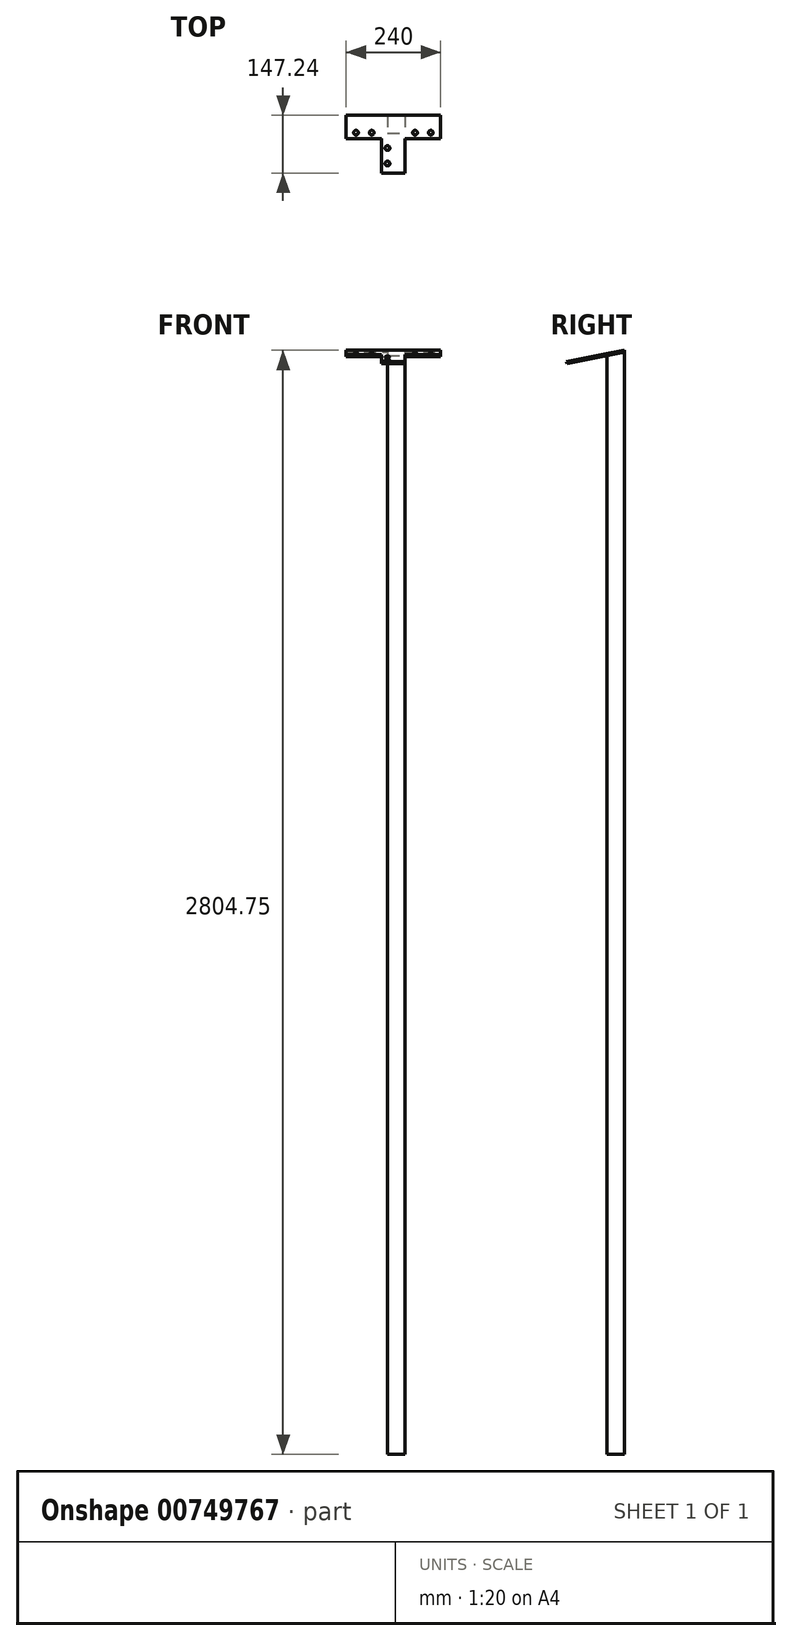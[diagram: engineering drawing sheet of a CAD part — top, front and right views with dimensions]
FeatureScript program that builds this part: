
annotation { "Feature Type Name" : "Feature", "Feature Type Description" : "" }
export const myFeature = defineFeature(function(context is Context, id is Id, definition is map)
    precondition{}
    {
        {
            var Q0;
            Q0=qCreatedBy(makeId("Top.planeOp"),FACE);
            var sketch = newSketch(context, id + "F0", { "sketchPlane" : qUnion([Q0])});
            skLineSegment(sketch, "E0.bottom", {"start": v(22.5, -22.5) * mm, "end": v(-22.5, -22.5) * mm});
            skLineSegment(sketch, "E0.top", {"start": v(22.5, 22.5) * mm, "end": v(-22.5, 22.5) * mm});
            skLineSegment(sketch, "E0.left", {"start": v(22.5, -22.5) * mm, "end": v(22.5, 22.5) * mm});
            skLineSegment(sketch, "E0.right", {"start": v(-22.5, -22.5) * mm, "end": v(-22.5, 22.5) * mm});
            skPoint(sketch, "E0.middle", {"position": v(0, 0) * mm});
            skSolve(sketch);
        }
        {
            var Q0;
            Q0=qSketchRegion(id+"F0",true);
            extrude(context, id + "F1", {"entities" : qUnion([Q0]), "depth" : 3330 * mm, "offsetDistance" : 25 * mm});
        }
        {
            var Q0;
            Q0=qCreatedBy(makeId("Top.planeOp"),FACE);
            cPlane(context, id + "F2", {"entities" : qUnion([Q0]), "cplaneType" : CPlaneType.OFFSET, "offset" : 965 * mm, "width" : 150 * mm, "height" : 150 * mm});
        }
        {
            var Q0;
            Q0=qCreatedBy(id+"F2.planeOp",FACE);
            var sketch = newSketch(context, id + "F3", { "sketchPlane" : qUnion([Q0])});
            skLineSegment(sketch, "E1", {"start": v(0, 0) * mm, "end": v(22.5, 0) * mm});
            skLineSegment(sketch, "E2", {"start": v(22.5, 0) * mm, "end": v(32.5, 0) * mm});
            skCircle(sketch, "E3", {"center": v(32.5, 0) * mm, "radius": 10 * mm});
            skLineSegment(sketch, "E4", {"start": v(32.5, 0) * mm, "end": v(32.5, 2) * mm});
            skLineSegment(sketch, "E5", {"start": v(32.5, 0) * mm, "end": v(32.5, -2) * mm});
            skLineSegment(sketch, "E6", {"start": v(32.5, -2) * mm, "end": v(22.5, -2) * mm});
            skLineSegment(sketch, "E7", {"start": v(32.5, 2) * mm, "end": v(22.5, 2) * mm});
            skLineSegment(sketch, "E8", {"start": v(0, 0) * mm, "end": v(-22.5, 0) * mm});
            skLineSegment(sketch, "E9", {"start": v(-22.5, 0) * mm, "end": v(-32.5, 0) * mm});
            skCircle(sketch, "E10", {"center": v(-32.5, 0) * mm, "radius": 10 * mm});
            skSolve(sketch);
        }
        {
            var Q0;
            Q0=makeQuery(id+"F1.opExtrude","CAP_EDGE",EDGE,{"disambiguationData":[OSD([sQuery(id+"F0.wireOp",EDGE,"E0.bottom")])],"isStart":false});
            cPlane(context, id + "F4", {"entities" : qUnion([Q0]), "cplaneType" : CPlaneType.LINE_ANGLE, "offset" : 25 * mm, "angle" : 101 * degree, "oppositeDirection" : true, "width" : 150 * mm, "height" : 150 * mm});
        }
        {
            var Q0;
            Q0=makeQuery(id+"F1.opExtrude","CAP_FACE",FACE,{"disambiguationData":[OSD([sQuery(id+"F0.wireOp",EDGE,"E0.bottom"),sQuery(id+"F0.wireOp",EDGE,"E0.top"),sQuery(id+"F0.wireOp",EDGE,"E0.left"),sQuery(id+"F0.wireOp",EDGE,"E0.right")])],"isStart":false});
            var sketch = newSketch(context, id + "F5", { "sketchPlane" : qUnion([Q0])});
            skLineSegment(sketch, "E11.bottom", {"start": v(-22.5, 22.5) * mm, "end": v(22.5, 22.5) * mm});
            skLineSegment(sketch, "E11.top", {"start": v(-22.5, -22.5) * mm, "end": v(22.5, -22.5) * mm});
            skLineSegment(sketch, "E11.left", {"start": v(-22.5, 22.5) * mm, "end": v(-22.5, -22.5) * mm});
            skLineSegment(sketch, "E11.right", {"start": v(22.5, 22.5) * mm, "end": v(22.5, -22.5) * mm});
            skSolve(sketch);
        }
        {
            var Q0;
            Q0=qCreatedBy(id+"F4.planeOp",FACE);
            var sketch = newSketch(context, id + "F6", { "sketchPlane" : qUnion([Q0])});
            skLineSegment(sketch, "E12.bottom", {"start": v(-22.5, -659.15) * mm, "end": v(22.5, -659.15) * mm});
            skLineSegment(sketch, "E12.top", {"start": v(-22.5, -613.3) * mm, "end": v(22.5, -613.3) * mm});
            skLineSegment(sketch, "E12.left", {"start": v(-22.5, -659.15) * mm, "end": v(-22.5, -613.3) * mm});
            skLineSegment(sketch, "E12.right", {"start": v(22.5, -659.15) * mm, "end": v(22.5, -613.3) * mm});
            skSolve(sketch);
        }
        {
            var Q0;
            Q0=makeQuery(id+"F6.imprint","IMPRINT",FACE,{"disambiguationData":[TD([[makeQuery(id+"F6.imprint","IMPRINT",EDGE,{"derivedFrom":sQuery(id+"F6.wireOp",EDGE,"E12.bottom")}),1.0]])]});
            extrude(context, id + "F7", {"entities" : qUnion([Q0]), "operationType" : NewBodyOperationType.ADD, "depth" : 25 * mm, "offsetDistance" : 25 * mm});
        }
        {
            var Q0;
            Q0=qCreatedBy(id+"F4.planeOp",FACE);
            var sketch = newSketch(context, id + "F8", { "sketchPlane" : qUnion([Q0])});
            skLineSegment(sketch, "E13.bottom", {"start": v(-37.5, -659.15) * mm, "end": v(22.5, -659.15) * mm});
            skLineSegment(sketch, "E13.top", {"start": v(-37.5, -599.15) * mm, "end": v(22.5, -599.15) * mm});
            skLineSegment(sketch, "E13.left", {"start": v(-37.5, -659.15) * mm, "end": v(-37.5, -599.15) * mm});
            skLineSegment(sketch, "E13.right", {"start": v(22.5, -659.15) * mm, "end": v(22.5, -599.15) * mm});
            skLineSegment(sketch, "E14.bottom", {"start": v(22.5, -659.15) * mm, "end": v(112.5, -659.15) * mm});
            skLineSegment(sketch, "E14.top", {"start": v(22.5, -599.15) * mm, "end": v(112.5, -599.15) * mm});
            skLineSegment(sketch, "E14.right", {"start": v(112.5, -659.15) * mm, "end": v(112.5, -599.15) * mm});
            skLineSegment(sketch, "E15.top", {"start": v(-37.5, -509.15) * mm, "end": v(22.5, -509.15) * mm});
            skLineSegment(sketch, "E15.left", {"start": v(-37.5, -599.15) * mm, "end": v(-37.5, -509.15) * mm});
            skLineSegment(sketch, "E15.right", {"start": v(22.5, -599.15) * mm, "end": v(22.5, -509.15) * mm});
            skLineSegment(sketch, "E16", {"start": v(-37.5, -659.15) * mm, "end": v(-37.5, -509.15) * mm});
            skLineSegment(sketch, "E17", {"start": v(-37.5, -659.15) * mm, "end": v(-127.5, -659.15) * mm});
            skLineSegment(sketch, "E18", {"start": v(-127.5, -659.15) * mm, "end": v(-127.5, -599.15) * mm});
            skLineSegment(sketch, "E19", {"start": v(-127.5, -599.15) * mm, "end": v(-37.5, -599.15) * mm});
            skPoint(sketch, "E20", {"position": v(7.5, -659.15) * mm});
            skSolve(sketch);
        }
        {
            var Q0;
            Q0=qSketchRegion(id+"F8",true);
            extrude(context, id + "F9", {"entities" : qUnion([Q0]), "operationType" : NewBodyOperationType.ADD, "depth" : 5 * mm, "offsetDistance" : 25 * mm});
        }
        {
            var Q0;
            Q0=makeQuery(id+"F9.boolean.opBoolean","MERGE",FACE,{"derivedFrom":[makeQuery(id+"F7.opExtrude","CAP_FACE",FACE,{"disambiguationData":[OSD([sQuery(id+"F6.wireOp",EDGE,"E12.bottom"),sQuery(id+"F6.wireOp",EDGE,"E12.top"),sQuery(id+"F6.wireOp",EDGE,"E12.left"),sQuery(id+"F6.wireOp",EDGE,"E12.right")])],"isStart":true}),makeQuery(id+"F9.opExtrude","CAP_FACE",FACE,{"disambiguationData":[OSD([sQuery(id+"F8.wireOp",EDGE,"E13.bottom"),sQuery(id+"F8.wireOp",EDGE,"E14.bottom"),sQuery(id+"F8.wireOp",EDGE,"E14.top"),sQuery(id+"F8.wireOp",EDGE,"E14.right"),sQuery(id+"F8.wireOp",EDGE,"E15.top"),sQuery(id+"F8.wireOp",EDGE,"E15.right"),sQuery(id+"F8.wireOp",EDGE,"E16")])],"isStart":true})]});
            var sketch = newSketch(context, id + "F10", { "sketchPlane" : qUnion([Q0])});
            skLineSegment(sketch, "E21", {"start": v(22.5, 509.15) * mm, "end": v(22.5, 534.15) * mm});
            skLineSegment(sketch, "E22", {"start": v(112.5, 599.15) * mm, "end": v(87.5, 599.15) * mm});
            skLineSegment(sketch, "E23", {"start": v(87.5, 599.15) * mm, "end": v(87.5, 614.15) * mm});
            skLineSegment(sketch, "E24", {"start": v(87.5, 614.15) * mm, "end": v(47.5, 614.15) * mm});
            skCircle(sketch, "E25", {"center": v(87.5, 614.15) * mm, "radius": 6 * mm});
            skCircle(sketch, "E26", {"center": v(47.5, 614.15) * mm, "radius": 6 * mm});
            skLineSegment(sketch, "E27", {"start": v(-22.5, 509.15) * mm, "end": v(-22.5, 602.33) * mm});
            skCircle(sketch, "E28.MirrorC", {"center": v(-22.5, 574.15) * mm, "radius": 6 * mm});
            skCircle(sketch, "E29.MirrorC", {"center": v(-22.5, 534.15) * mm, "radius": 6 * mm});
            skLineSegment(sketch, "E30", {"start": v(-7.5, 509.15) * mm, "end": v(-7.5, 574.6) * mm, "construction": true});
            skCircle(sketch, "E31.MirrorC", {"center": v(-62.5, 614.15) * mm, "radius": 6 * mm});
            skCircle(sketch, "E32.MirrorC", {"center": v(-102.5, 614.15) * mm, "radius": 6 * mm});
            skSolve(sketch);
        }
        {
            var Q0;
            Q0=qSketchRegion(id+"F10",true);
            extrude(context, id + "F11", {"entities" : qUnion([Q0]), "operationType" : NewBodyOperationType.REMOVE, "oppositeDirection" : true, "depth" : 25 * mm, "offsetDistance" : 25 * mm});
        }
        {
            var Q0;
            Q0=qCreatedBy(makeId("Top.planeOp"),FACE);
            var sketch = newSketch(context, id + "F12", { "sketchPlane" : qUnion([Q0])});
            skLineSegment(sketch, "E33.bottom", {"start": v(-22.5, 22.5) * mm, "end": v(127.5, 22.5) * mm});
            skLineSegment(sketch, "E33.top", {"start": v(-22.5, 27.27) * mm, "end": v(127.5, 27.27) * mm});
            skLineSegment(sketch, "E33.left", {"start": v(-22.5, 22.5) * mm, "end": v(-22.5, 27.27) * mm});
            skLineSegment(sketch, "E33.right", {"start": v(127.5, 22.5) * mm, "end": v(127.5, 27.27) * mm});
            skSolve(sketch);
        }
        {
            var Q0;
            Q0=qSketchRegion(id+"F12",true);
            extrude(context, id + "F13", {"entities" : qUnion([Q0]), "operationType" : NewBodyOperationType.REMOVE, "depth" : 3358.7 * mm, "offsetDistance" : 25 * mm});
        }
        {
            var Q0;
            Q0=makeQuery(id+"F13.boolean.opBoolean","COPY",FACE,{"derivedFrom":makeQuery(id+"F13.opExtrude","SWEPT_FACE",FACE,{"disambiguationData":[OSD([sQuery(id+"F12.wireOp",EDGE,"E33.left")])]})});
            var sketch = newSketch(context, id + "F14", { "sketchPlane" : qUnion([Q0])});
            skLineSegment(sketch, "E34", {"start": v(22.5, 3333.65) * mm, "end": v(23.45, 3333.84) * mm});
            skLineSegment(sketch, "E35", {"start": v(23.45, 3333.84) * mm, "end": v(22.5, 3338.75) * mm});
            skLineSegment(sketch, "E36", {"start": v(22.5, 3338.75) * mm, "end": v(22.5, 3333.65) * mm});
            skSolve(sketch);
        }
        {
            var Q0;
            Q0=qSketchRegion(id+"F14",true);
            extrude(context, id + "F15", {"entities" : qUnion([Q0]), "operationType" : NewBodyOperationType.REMOVE, "oppositeDirection" : true, "depth" : 106.2 * mm, "offsetDistance" : 25 * mm});
        }
        {
            var Q0;
            Q0=makeQuery(id+"F1.opExtrude","CAP_FACE",FACE,{"disambiguationData":[OSD([sQuery(id+"F0.wireOp",EDGE,"E0.bottom"),sQuery(id+"F0.wireOp",EDGE,"E0.top"),sQuery(id+"F0.wireOp",EDGE,"E0.left"),sQuery(id+"F0.wireOp",EDGE,"E0.right")])],"isStart":true});
            var sketch = newSketch(context, id + "F16", { "sketchPlane" : qUnion([Q0])});
            skLineSegment(sketch, "E37.bottom", {"start": v(-22.5, 22.5) * mm, "end": v(22.5, 22.5) * mm});
            skLineSegment(sketch, "E37.top", {"start": v(-22.5, -22.5) * mm, "end": v(22.5, -22.5) * mm});
            skLineSegment(sketch, "E37.left", {"start": v(-22.5, 22.5) * mm, "end": v(-22.5, -22.5) * mm});
            skLineSegment(sketch, "E37.right", {"start": v(22.5, 22.5) * mm, "end": v(22.5, -22.5) * mm});
            skSolve(sketch);
        }
        {
            var Q0;
            Q0 = qSketchRegion(id + "F16", true);
            extrude(context, id + "F17", {"entities" : qUnion([Q0]), "operationType" : NewBodyOperationType.REMOVE, "oppositeDirection" : true, "depth" : 534 * mm, "offsetDistance" : 25 * mm});
        }
    });
